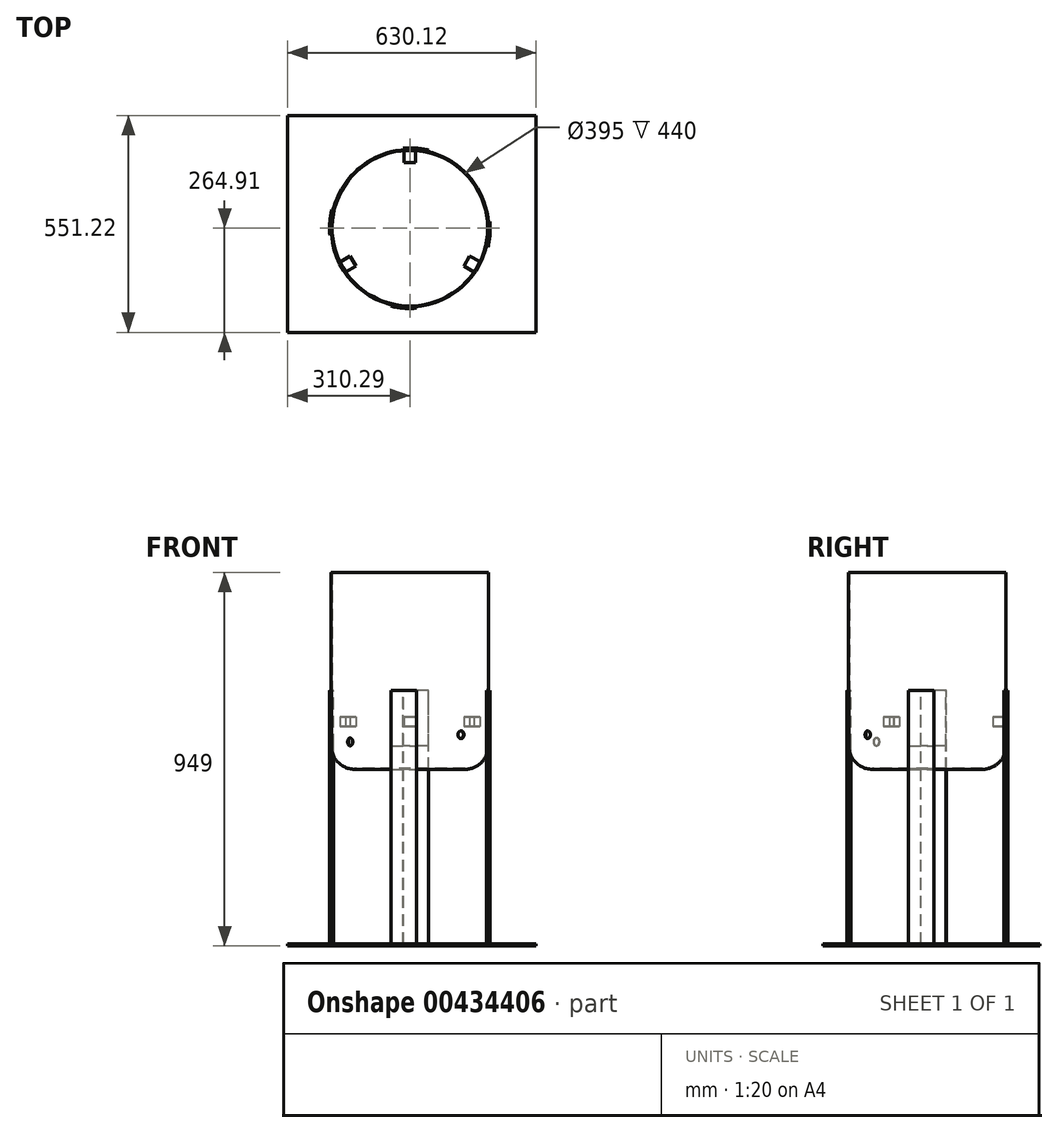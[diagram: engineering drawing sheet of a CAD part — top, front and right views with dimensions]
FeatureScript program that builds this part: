
annotation { "Feature Type Name" : "Feature", "Feature Type Description" : "" }
export const myFeature = defineFeature(function(context is Context, id is Id, definition is map)
    precondition{}
    {
        {
            var Q0;
            Q0=qCreatedBy(makeId("Top.planeOp"),FACE);
            var sketch = newSketch(context, id + "F0", { "sketchPlane" : qUnion([Q0])});
            skCircle(sketch, "E0", {"center": v(0, 0) * mm, "radius": 200 * mm});
            skSolve(sketch);
        }
        {
            var Q0;
            Q0 = qSketchRegion(id + "F0", true);
            extrude(context, id + "F1", {"entities" : qUnion([Q0]), "depth" : 500 * mm});
        }
        {
            var Q0;
            Q0=makeQuery(id+"F1.opExtrude","CAP_EDGE",EDGE,{"disambiguationData":[OSD([sQuery(id+"F0.wireOp",EDGE,"E0")])],"isStart":true});
            fillet(context, id + "F2", {"entities" : qUnion([Q0]), "radius" : 60 * mm, "tangentPropagation" : true, "allowEdgeOverflow" : false});
        }
        {
            var Q0;
            Q0=makeQuery(id+"F1.opExtrude","CAP_FACE",FACE,{"disambiguationData":[OSD([sQuery(id+"F0.wireOp",EDGE,"E0")])],"isStart":false});
            shell(context, id + "F3", {"entities" : qUnion([Q0]), "thickness" : 2.5 * mm});
        }
        {
            var Q0;
            Q0=qCreatedBy(makeId("Top.planeOp"),FACE);
            cPlane(context, id + "F4", {"entities" : qUnion([Q0]), "cplaneType" : CPlaneType.OFFSET, "offset" : 200 * mm, "width" : 150 * mm, "height" : 150 * mm});
        }
        {
            var Q0;
            Q0=qCreatedBy(id+"F4.planeOp",FACE);
            var sketch = newSketch(context, id + "F5", { "sketchPlane" : qUnion([Q0])});
            skArc(sketch, "E1", {"start": v(194.43, -46.86) * mm, "mid": v(199.41, -15.33) * mm, "end": v(199.31, 16.59) * mm});
            skLineSegment(sketch, "E2", {"start": v(199.31, 16.59) * mm, "end": v(203.3, 16.92) * mm});
            skLineSegment(sketch, "E3", {"start": v(194.43, -46.86) * mm, "end": v(198.32, -47.8) * mm});
            skArc(sketch, "E4", {"start": v(198.32, -47.8) * mm, "mid": v(203.4, -15.64) * mm, "end": v(203.3, 16.92) * mm});
            skArc(sketch, "E5.1.0", {"start": v(46.86, 194.43) * mm, "mid": v(15.33, 199.41) * mm, "end": v(-16.59, 199.31) * mm});
            skLineSegment(sketch, "E5.1.1", {"start": v(46.86, 194.43) * mm, "end": v(47.8, 198.32) * mm});
            skLineSegment(sketch, "E5.1.2", {"start": v(-16.59, 199.31) * mm, "end": v(-16.92, 203.3) * mm});
            skArc(sketch, "E5.1.3", {"start": v(47.8, 198.32) * mm, "mid": v(15.64, 203.4) * mm, "end": v(-16.92, 203.3) * mm});
            skArc(sketch, "E5.2.0", {"start": v(-194.43, 46.86) * mm, "mid": v(-199.41, 15.33) * mm, "end": v(-199.31, -16.59) * mm});
            skLineSegment(sketch, "E5.2.1", {"start": v(-194.43, 46.86) * mm, "end": v(-198.32, 47.8) * mm});
            skLineSegment(sketch, "E5.2.2", {"start": v(-199.31, -16.59) * mm, "end": v(-203.3, -16.92) * mm});
            skArc(sketch, "E5.2.3", {"start": v(-198.32, 47.8) * mm, "mid": v(-203.4, 15.64) * mm, "end": v(-203.3, -16.92) * mm});
            skArc(sketch, "E5.3.0", {"start": v(-46.86, -194.43) * mm, "mid": v(-15.33, -199.41) * mm, "end": v(16.59, -199.31) * mm});
            skLineSegment(sketch, "E5.3.1", {"start": v(-46.86, -194.43) * mm, "end": v(-47.8, -198.32) * mm});
            skLineSegment(sketch, "E5.3.2", {"start": v(16.59, -199.31) * mm, "end": v(16.92, -203.3) * mm});
            skArc(sketch, "E5.3.3", {"start": v(-47.8, -198.32) * mm, "mid": v(-15.64, -203.4) * mm, "end": v(16.92, -203.3) * mm});
            skSolve(sketch);
        }
        {
            var Q0;
            Q0 = qSketchRegion(id + "F5", true);
            extrude(context, id + "F6", {"entities" : qUnion([Q0]), "operationType" : NewBodyOperationType.ADD, "oppositeDirection" : true, "depth" : 644 * mm});
        }
        {
            var Q0;
            Q0=makeQuery(id+"F6.opExtrude","CAP_FACE",FACE,{"disambiguationData":[OSD([sQuery(id+"F5.wireOp",EDGE,"E5.2.0"),sQuery(id+"F5.wireOp",EDGE,"E5.2.1"),sQuery(id+"F5.wireOp",EDGE,"E5.2.2"),sQuery(id+"F5.wireOp",EDGE,"E5.2.3")])],"isStart":false});
            var sketch = newSketch(context, id + "F7", { "sketchPlane" : qUnion([Q0])});
            skLineSegment(sketch, "E6.bottom", {"start": v(-310.29, 264.91) * mm, "end": v(319.83, 264.91) * mm});
            skLineSegment(sketch, "E6.top", {"start": v(-310.29, -286.31) * mm, "end": v(319.83, -286.31) * mm});
            skLineSegment(sketch, "E6.left", {"start": v(-310.29, 264.91) * mm, "end": v(-310.29, -286.31) * mm});
            skLineSegment(sketch, "E6.right", {"start": v(319.83, 264.91) * mm, "end": v(319.83, -286.31) * mm});
            skSolve(sketch);
        }
        {
            var Q0;
            Q0 = qSketchRegion(id + "F7", true);
            extrude(context, id + "F8", {"entities" : qUnion([Q0]), "operationType" : NewBodyOperationType.ADD, "depth" : 5 * mm});
        }
        {
            var Q0;
            {var subQ0=sQuery(id+"F5.wireOp",EDGE,"E5.3.2");Q0=makeQuery(id+"F6.boolean.opBoolean","SPLIT",EDGE,{"disambiguationData":[topologyDisambiguationEdgeConnected([makeQuery(id+"F1.opExtrude","SWEPT_FACE",FACE,{"disambiguationData":[OSD([sQuery(id+"F0.wireOp",EDGE,"E0")])]})])],"derivedFrom":makeQuery(id+"F6.opExtrude","SWEPT_EDGE",EDGE,{"disambiguationData":[OSD([sQuery(id+"F5.wireOp",EDGE,"E5.3.0"),subQ0])]})});}
            cPoint(context, id + "F9", {"entities" : qUnion([Q0]), "parameter" : 0.5});
        }
        {
            var Q0;
            Q0=makeQuery(id+"F6.opExtrude","CAP_VERTEX",VERTEX,{"disambiguationData":[OSD([sQuery(id+"F5.wireOp",EDGE,"E5.3.0"),sQuery(id+"F5.wireOp",EDGE,"E5.3.2")])],"isStart":true});
            var Q1;
            Q1 = qCreatedBy(id + "F9" ,VERTEX);
            var Q2;
            Q2=makeQuery(id+"F6.opExtrude","CAP_VERTEX",VERTEX,{"disambiguationData":[OSD([sQuery(id+"F5.wireOp",EDGE,"E1"),sQuery(id+"F5.wireOp",EDGE,"E3")])],"isStart":true});
            cPlane(context, id + "F10", {"entities" : qUnion([Q0, Q1, Q2]), "cplaneType" : CPlaneType.THREE_POINT, "offset" : 25 * mm, "width" : 150 * mm, "height" : 150 * mm});
        }
        {
            var Q0;
            Q0=qCreatedBy(id+"F10.planeOp",FACE);
            var sketch = newSketch(context, id + "F11", { "sketchPlane" : qUnion([Q0])});
            skLineSegment(sketch, "E7.0", {"start": v(117.12, 60) * mm, "end": v(117.12, 200) * mm});
            skLineSegment(sketch, "E8.0", {"start": v(-117.12, 60) * mm, "end": v(-117.12, 200) * mm});
            skLineSegment(sketch, "E9", {"start": v(117.12, 87.82) * mm, "end": v(-117.12, 87.82) * mm});
            skCircle(sketch, "E10", {"center": v(0, 87.82) * mm, "radius": 10 * mm});
            skSolve(sketch);
        }
        {
            var Q0;
            Q0 = qSketchRegion(id + "F11", true);
            extrude(context, id + "F12", {"entities" : qUnion([Q0]), "operationType" : NewBodyOperationType.REMOVE, "oppositeDirection" : true, "depth" : 230 * mm});
        }
        {
            var Q0;
            {var subQ0=sQuery(id+"F5.wireOp",EDGE,"E5.2.2");Q0=makeQuery(id+"F6.boolean.opBoolean","SPLIT",EDGE,{"disambiguationData":[topologyDisambiguationEdgeConnected([makeQuery(id+"F1.opExtrude","SWEPT_FACE",FACE,{"disambiguationData":[OSD([sQuery(id+"F0.wireOp",EDGE,"E0")])]})])],"derivedFrom":makeQuery(id+"F6.opExtrude","SWEPT_EDGE",EDGE,{"disambiguationData":[OSD([sQuery(id+"F5.wireOp",EDGE,"E5.2.0"),subQ0])]})});}
            cPoint(context, id + "F13", {"entities" : qUnion([Q0]), "parameter" : 0.5});
        }
        {
            var Q0;
            Q0=makeQuery(id+"F6.opExtrude","CAP_VERTEX",VERTEX,{"disambiguationData":[OSD([sQuery(id+"F5.wireOp",EDGE,"E5.2.0"),sQuery(id+"F5.wireOp",EDGE,"E5.2.2")])],"isStart":true});
            var Q1;
            Q1 = qCreatedBy(id + "F13" ,VERTEX);
            var Q2;
            Q2=makeQuery(id+"F6.opExtrude","CAP_VERTEX",VERTEX,{"disambiguationData":[OSD([sQuery(id+"F5.wireOp",EDGE,"E5.3.0"),sQuery(id+"F5.wireOp",EDGE,"E5.3.1")])],"isStart":true});
            cPlane(context, id + "F14", {"entities" : qUnion([Q0, Q1, Q2]), "cplaneType" : CPlaneType.THREE_POINT, "offset" : 25 * mm, "width" : 150 * mm, "height" : 150 * mm});
        }
        {
            var Q0;
            Q0=qCreatedBy(id+"F14.planeOp",FACE);
            var sketch = newSketch(context, id + "F15", { "sketchPlane" : qUnion([Q0])});
            skLineSegment(sketch, "E11.0", {"start": v(117.12, 60) * mm, "end": v(117.12, 200) * mm});
            skLineSegment(sketch, "E12.0", {"start": v(-117.12, 60) * mm, "end": v(-117.12, 200) * mm});
            skLineSegment(sketch, "E13", {"start": v(117.12, 69.75) * mm, "end": v(-117.12, 69.75) * mm});
            skCircle(sketch, "E14", {"center": v(0, 69.75) * mm, "radius": 10 * mm});
            skSolve(sketch);
        }
        {
            var Q0;
            Q0 = qSketchRegion(id + "F15", true);
            extrude(context, id + "F16", {"entities" : qUnion([Q0]), "operationType" : NewBodyOperationType.REMOVE, "oppositeDirection" : true, "depth" : 560.1 * mm});
        }
        {
            var Q0;
            {var subQ0=sQuery(id+"F0.wireOp",EDGE,"E0");Q0=makeQuery(id+"F3.opShell","OFFSET_FACE",FACE,{"disambiguationData":[OSD([subQ0]),TDD([makeQuery(id+"F1.opExtrude","CAP_FACE",FACE,{"disambiguationData":[OSD([subQ0])],"isStart":true})])]});}
            cPlane(context, id + "F17", {"entities" : qUnion([Q0]), "cplaneType" : CPlaneType.OFFSET, "offset" : 106 * mm, "width" : 150 * mm, "height" : 150 * mm});
        }
        {
            var Q0;
            Q0=qCreatedBy(id+"F17.planeOp",FACE);
            var sketch = newSketch(context, id + "F18", { "sketchPlane" : qUnion([Q0])});
            skCircle(sketch, "E15.0", {"center": v(0, 0) * mm, "radius": 197.5 * mm});
            skArc(sketch, "E16", {"start": v(14.79, 196.95) * mm, "mid": v(-0.15, 197.5) * mm, "end": v(-15.09, 196.92) * mm});
            skLineSegment(sketch, "E17", {"start": v(-15.09, 196.92) * mm, "end": v(-15.09, 166.95) * mm});
            skLineSegment(sketch, "E18", {"start": v(-15.09, 166.95) * mm, "end": v(14.79, 166.95) * mm});
            skLineSegment(sketch, "E19", {"start": v(14.79, 166.95) * mm, "end": v(14.79, 196.95) * mm});
            skLineSegment(sketch, "E20.1.0", {"start": v(-163, -111.53) * mm, "end": v(-137.04, -96.54) * mm});
            skArc(sketch, "E20.1.1", {"start": v(-177.95, -85.66) * mm, "mid": v(-170.96, -98.87) * mm, "end": v(-163, -111.53) * mm});
            skLineSegment(sketch, "E20.1.2", {"start": v(-151.97, -70.66) * mm, "end": v(-177.95, -85.66) * mm});
            skLineSegment(sketch, "E20.1.3", {"start": v(-137.04, -96.54) * mm, "end": v(-151.97, -70.66) * mm});
            skLineSegment(sketch, "E20.2.0", {"start": v(178.08, -85.4) * mm, "end": v(152.12, -70.4) * mm});
            skArc(sketch, "E20.2.1", {"start": v(163.16, -111.28) * mm, "mid": v(171.1, -98.62) * mm, "end": v(178.08, -85.4) * mm});
            skLineSegment(sketch, "E20.2.2", {"start": v(137.18, -96.28) * mm, "end": v(163.16, -111.28) * mm});
            skLineSegment(sketch, "E20.2.3", {"start": v(152.12, -70.4) * mm, "end": v(137.18, -96.28) * mm});
            skSolve(sketch);
        }
        {
            var Q0;
            {var subQ0=sQuery(id+"F18.wireOp",EDGE,"E16");Q0=makeQuery(id+"F18.imprint","IMPRINT",FACE,{"disambiguationData":[TD([[makeQuery(id+"F18.imprint","IMPRINT",EDGE,{"derivedFrom":subQ0}),-1.0]])]});}
            var Q1;
            {var subQ0=sQuery(id+"F18.wireOp",EDGE,"E20.1.1");Q1=makeQuery(id+"F18.imprint","IMPRINT",FACE,{"disambiguationData":[TD([[makeQuery(id+"F18.imprint","IMPRINT",EDGE,{"derivedFrom":subQ0}),-1.0]])]});}
            var Q2;
            {var subQ0=sQuery(id+"F18.wireOp",EDGE,"E20.2.1");Q2=makeQuery(id+"F18.imprint","IMPRINT",FACE,{"disambiguationData":[TD([[makeQuery(id+"F18.imprint","IMPRINT",EDGE,{"derivedFrom":subQ0}),-1.0]])]});}
            var Q3;
            Q3=makeQuery(id+"F18.imprint","IMPRINT",FACE,{"disambiguationData":[TD([[makeQuery(id+"F18.imprint","IMPRINT",EDGE,{"derivedFrom":sQuery(id+"F18.wireOp",EDGE,"E20.1.0")}),1.0]])]});
            var Q4;
            Q4=makeQuery(id+"F18.imprint","IMPRINT",FACE,{"disambiguationData":[TD([[makeQuery(id+"F18.imprint","IMPRINT",EDGE,{"derivedFrom":sQuery(id+"F18.wireOp",EDGE,"E20.2.0")}),1.0]])]});
            var Q5;
            Q5=makeQuery(id+"F18.imprint","IMPRINT",FACE,{"disambiguationData":[TD([[makeQuery(id+"F18.imprint","IMPRINT",EDGE,{"derivedFrom":sQuery(id+"F18.wireOp",EDGE,"E16")}),1.0]])]});
            extrude(context, id + "F19", {"entities" : qUnion([Q0, Q1, Q2, Q3, Q4, Q5]), "operationType" : NewBodyOperationType.ADD, "depth" : 25 * mm});
        }
    });
